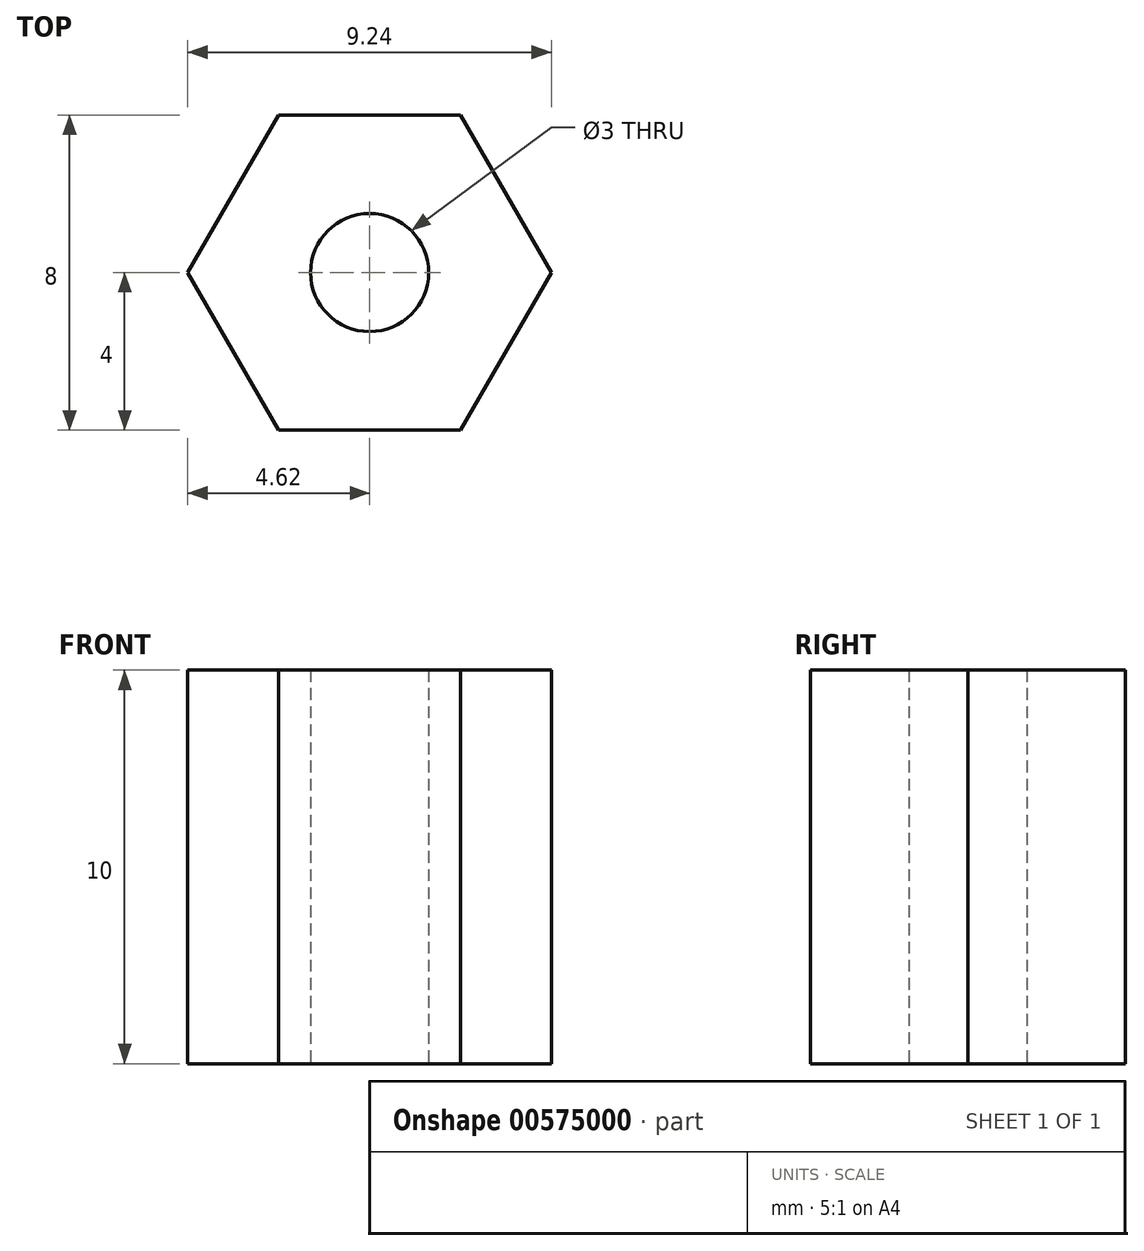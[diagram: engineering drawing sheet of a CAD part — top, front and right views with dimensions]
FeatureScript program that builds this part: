
annotation { "Feature Type Name" : "Feature", "Feature Type Description" : "" }
export const myFeature = defineFeature(function(context is Context, id is Id, definition is map)
    precondition{}
    {
        {
            var Q0;
            Q0=qCreatedBy(makeId("Top.planeOp"),FACE);
            var sketch = newSketch(context, id + "F0", { "sketchPlane" : qUnion([Q0])});
            skCircle(sketch, "E0.cCircle", {"center": v(0, 0) * mm, "radius": 4 * mm, "construction": true});
            skLineSegment(sketch, "E0.0", {"start": v(-2.3, 4) * mm, "end": v(2.3, 4) * mm});
            skLineSegment(sketch, "E0.1", {"start": v(2.3, 4) * mm, "end": v(4.62, 0) * mm});
            skLineSegment(sketch, "E0.2", {"start": v(4.62, 0) * mm, "end": v(2.3, -4) * mm});
            skLineSegment(sketch, "E0.3", {"start": v(2.3, -4) * mm, "end": v(-2.3, -4) * mm});
            skLineSegment(sketch, "E0.4", {"start": v(-2.3, -4) * mm, "end": v(-4.62, 0) * mm});
            skLineSegment(sketch, "E0.5", {"start": v(-4.62, 0) * mm, "end": v(-2.3, 4) * mm});
            skPoint(sketch, "E0.0.midPoint", {"position": v(0, 4) * mm});
            skCircle(sketch, "E1", {"center": v(0, 0) * mm, "radius": 1.5 * mm});
            skSolve(sketch);
        }
        {
            var Q0;
            Q0 = qSketchRegion(id + "F0", true);
            extrude(context, id + "F1", {"entities" : qUnion([Q0]), "depth" : 10 * mm, "offsetDistance" : 25 * mm});
        }
    });
